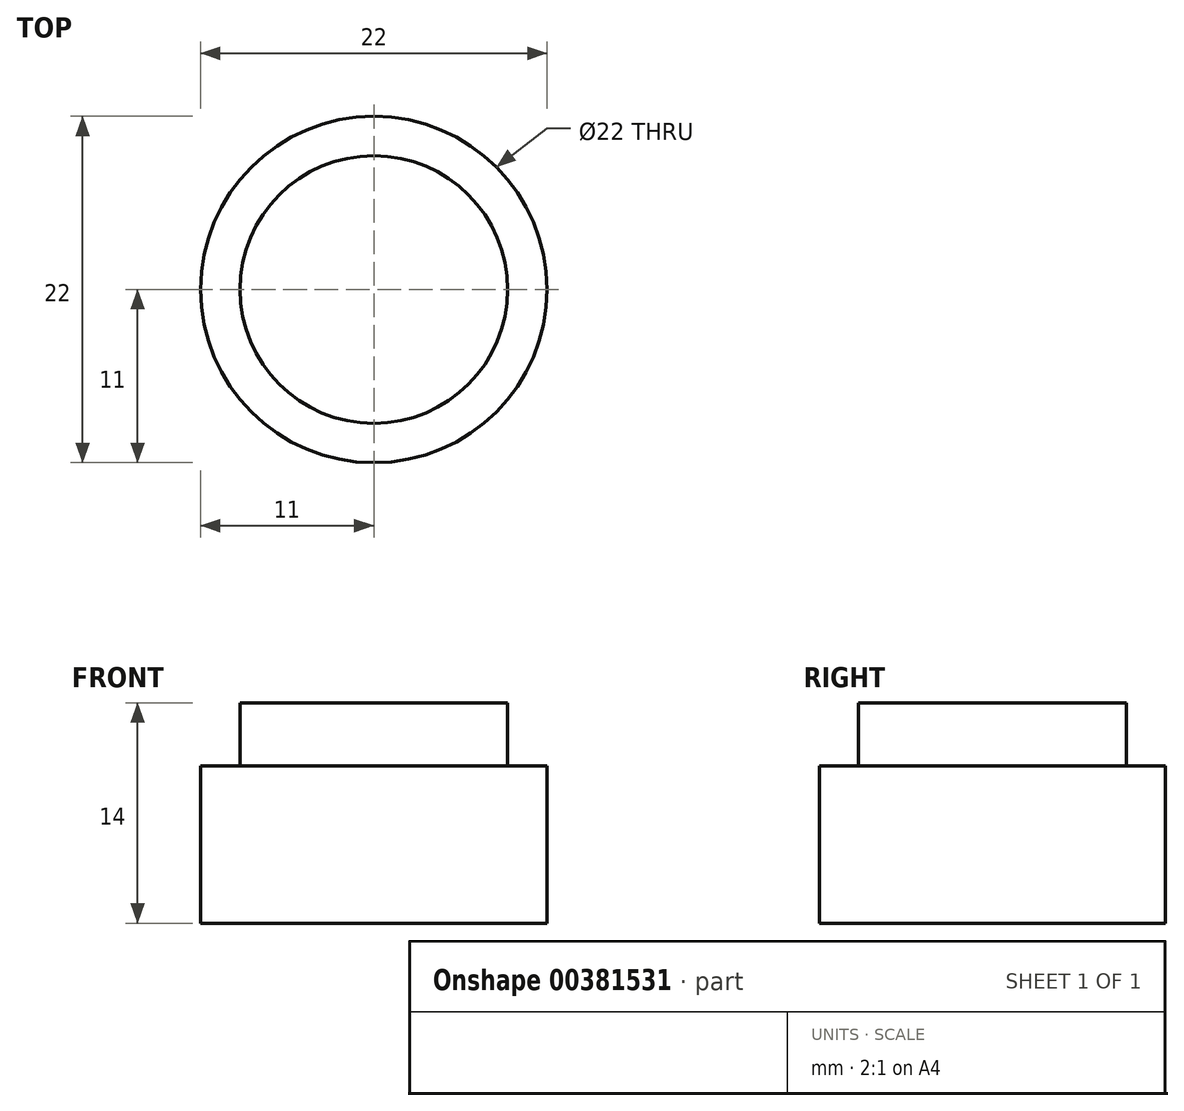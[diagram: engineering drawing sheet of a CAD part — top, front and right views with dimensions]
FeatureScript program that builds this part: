
annotation { "Feature Type Name" : "Feature", "Feature Type Description" : "" }
export const myFeature = defineFeature(function(context is Context, id is Id, definition is map)
    precondition{}
    {
        {
            var Q0;
            Q0=qCreatedBy(makeId("Top.planeOp"),FACE);
            var sketch = newSketch(context, id + "F0", { "sketchPlane" : qUnion([Q0])});
            skCircle(sketch, "E0", {"center": v(0, 0) * mm, "radius": 12.7 * mm});
            skCircle(sketch, "E1", {"center": v(0, 0) * mm, "radius": 20 * mm});
            skCircle(sketch, "E2", {"center": v(0, 0) * mm, "radius": 11 * mm});
            skCircle(sketch, "E3", {"center": v(0, 0) * mm, "radius": 8.5 * mm});
            skSolve(sketch);
        }
        {
            var Q0;
            Q0=sQuery(id+"F0.wireOp",EDGE,"E3");
            extrude(context, id + "F1", {"bodyType" : ToolBodyType.SURFACE, "surfaceEntities" : qUnion([Q0]), "depth" : 4 * mm});
        }
        {
            var Q0;
            Q0=sQuery(id+"F0.wireOp",EDGE,"E2");
            extrude(context, id + "F2", {"bodyType" : ToolBodyType.SURFACE, "surfaceEntities" : qUnion([Q0]), "oppositeDirection" : true, "depth" : 10 * mm});
        }
    });
